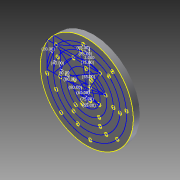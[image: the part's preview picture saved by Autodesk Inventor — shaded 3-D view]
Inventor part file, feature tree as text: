
AUTODESK INVENTOR PART (.ipt)
format: ipt  version: 2012 (Build 160160000, 160)  size: 190,976 bytes
history: native  units: in
note: dims shown in document units (in); Inventor stores cm internally (conversion verified against a paired STEP export)
features: sketch x2, extrude x1, hole x1
ambient origin geometry x8: Origin, YZ Plane, XZ Plane, XY Plane, X Axis, Y Axis, Z Axis, Center Point
feature tree (4):
  sketch  "Sketch3"  dims[d104=0.5in d105=0.5in]
  extrude  "Extrusion3"  Depth=0.5in
  hole  "Hole2"  [1 undecoded]
  sketch  "Sketch5"  dims[d106=0.5in d107=0.5in d108=0.5in d110=1.0in d111=0.2749in d112=0.2749in d113=0.2749in d114=0.2749in d115=0.2749in d116=3.1496in d118=360.0deg d120=2.7559in d122=360.0deg d124=2.3622in d126=360.0deg d128=1.9685in d130=360.0deg d132=1.5748in d134=360.0deg d136=1.1811in d138=360.0deg d140=0.5in d141=0.5in d142=0.0in d143=0.25in d144=0.75in d145=0.375in d146=0.25in d147=0.5635in d148=1.0in d149=0.8108in d155=0.1374in d156=0.2749in d157=60.0deg d158=0.5497in d159=0.5497in d160=60.0deg d161=3.0in d168=0.4466in d169=0.5841in d170=75.0deg d171=0.3779in d172=0.3779in d173=75.0deg]
note: 1 required parameter value undecoded (feature->parameter linkage not recoverable at this tier; creation-order binding heuristic only, values carry confidence <= 0.55)
